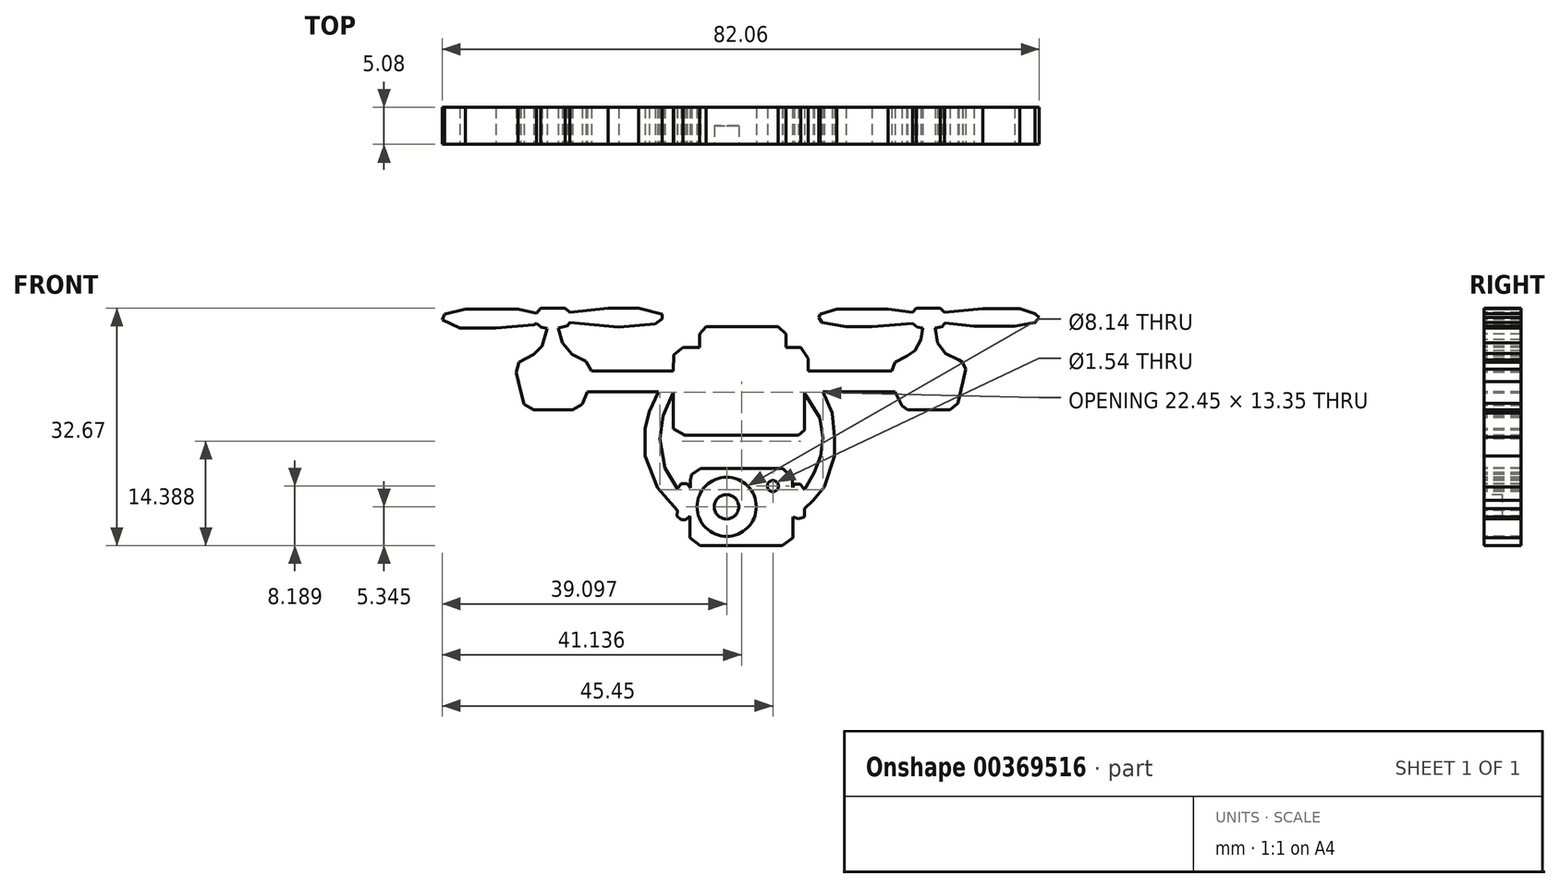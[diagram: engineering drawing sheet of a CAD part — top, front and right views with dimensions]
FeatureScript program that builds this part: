
annotation { "Feature Type Name" : "Feature", "Feature Type Description" : "" }
export const myFeature = defineFeature(function(context is Context, id is Id, definition is map)
    precondition{}
    {
        {
            var Q0;
            Q0=qCreatedBy(makeId("Front.planeOp"),FACE);
            var sketch = newSketch(context, id + "F0", { "sketchPlane" : qUnion([Q0])});
            skLineSegment(sketch, "E0", {"start": v(-9.35, 25.61) * mm, "end": v(-20.58, 25.61) * mm});
            skLineSegment(sketch, "E1", {"start": v(9.2, 25.61) * mm, "end": v(20.72, 25.61) * mm});
            skLineSegment(sketch, "E2", {"start": v(21.15, 22.74) * mm, "end": v(11.22, 22.74) * mm});
            skLineSegment(sketch, "E3", {"start": v(-11.37, 22.74) * mm, "end": v(-21.15, 22.74) * mm});
            skLineSegment(sketch, "E4", {"start": v(-23.17, 20.3) * mm, "end": v(-28.5, 20.3) * mm});
            skLineSegment(sketch, "E5", {"start": v(7.91, 16.77) * mm, "end": v(-7.76, 16.77) * mm});
            skLineSegment(sketch, "E6", {"start": v(9.2, 25.61) * mm, "end": v(9.2, 27.35) * mm});
            skLineSegment(sketch, "E7", {"start": v(9.2, 27.35) * mm, "end": v(8.22, 28.88) * mm});
            skLineSegment(sketch, "E8", {"start": v(8.22, 28.88) * mm, "end": v(6.18, 28.88) * mm});
            skLineSegment(sketch, "E9", {"start": v(6.18, 28.88) * mm, "end": v(6.18, 30.7) * mm});
            skLineSegment(sketch, "E10", {"start": v(6.18, 30.7) * mm, "end": v(5.06, 31.73) * mm});
            skLineSegment(sketch, "E11", {"start": v(5.06, 31.73) * mm, "end": v(-4.8, 31.73) * mm});
            skLineSegment(sketch, "E12", {"start": v(-4.8, 31.73) * mm, "end": v(-5.72, 30.7) * mm});
            skLineSegment(sketch, "E13", {"start": v(-5.72, 30.7) * mm, "end": v(-5.72, 28.88) * mm});
            skLineSegment(sketch, "E14", {"start": v(-5.72, 28.88) * mm, "end": v(-7.96, 28.88) * mm});
            skLineSegment(sketch, "E15", {"start": v(-7.96, 28.88) * mm, "end": v(-9.28, 27.86) * mm});
            skLineSegment(sketch, "E16", {"start": v(-9.28, 27.86) * mm, "end": v(-9.35, 25.61) * mm});
            skLineSegment(sketch, "E17", {"start": v(-7.76, 16.77) * mm, "end": v(-9.32, 17.68) * mm});
            skPoint(sketch, "E17.endSnap0", {"position": v(-9.32, 26.74) * mm});
            skLineSegment(sketch, "E18", {"start": v(-9.32, 17.68) * mm, "end": v(-9.32, 22.67) * mm});
            skLineSegment(sketch, "E19", {"start": v(-11.37, 22.74) * mm, "end": v(-12.64, 20.03) * mm});
            skLineSegment(sketch, "E20", {"start": v(-7.05, 5.68) * mm, "end": v(-7.05, 2.73) * mm});
            skLineSegment(sketch, "E21", {"start": v(-7.05, 2.73) * mm, "end": v(-5.62, 1.6) * mm});
            skLineSegment(sketch, "E22", {"start": v(-5.62, 1.6) * mm, "end": v(5.67, 1.6) * mm});
            skLineSegment(sketch, "E23", {"start": v(5.67, 1.6) * mm, "end": v(7.1, 2.73) * mm});
            skLineSegment(sketch, "E24", {"start": v(7.1, 2.73) * mm, "end": v(7.1, 5.58) * mm});
            skLineSegment(sketch, "E25", {"start": v(11.22, 22.74) * mm, "end": v(12.55, 19.85) * mm});
            skLineSegment(sketch, "E26", {"start": v(11.45, 9.68) * mm, "end": v(12.85, 13.92) * mm});
            skLineSegment(sketch, "E27", {"start": v(12.85, 13.92) * mm, "end": v(12.85, 16.52) * mm});
            skLineSegment(sketch, "E28", {"start": v(12.85, 16.52) * mm, "end": v(12.55, 19.85) * mm});
            skLineSegment(sketch, "E29", {"start": v(8.74, 9.32) * mm, "end": v(10.07, 11.62) * mm});
            skLineSegment(sketch, "E30", {"start": v(10.07, 11.62) * mm, "end": v(10.92, 13.92) * mm});
            skLineSegment(sketch, "E31", {"start": v(8.7, 22.54) * mm, "end": v(10.8, 19.19) * mm});
            skLineSegment(sketch, "E32", {"start": v(10.8, 19.19) * mm, "end": v(11.28, 16.4) * mm});
            skLineSegment(sketch, "E33", {"start": v(11.28, 16.4) * mm, "end": v(10.92, 13.92) * mm});
            skLineSegment(sketch, "E34", {"start": v(-12.64, 20.03) * mm, "end": v(-13.22, 17.68) * mm});
            skLineSegment(sketch, "E35", {"start": v(-13.22, 17.68) * mm, "end": v(-13.22, 13.92) * mm});
            skLineSegment(sketch, "E36", {"start": v(-13.22, 13.92) * mm, "end": v(-11.47, 9.57) * mm});
            skLineSegment(sketch, "E37", {"start": v(-11.47, 9.57) * mm, "end": v(-8.75, 6.42) * mm});
            skLineSegment(sketch, "E38", {"start": v(-8.75, 9.45) * mm, "end": v(-10.44, 12.29) * mm});
            skLineSegment(sketch, "E39", {"start": v(-10.44, 12.29) * mm, "end": v(-11.17, 16.28) * mm});
            skLineSegment(sketch, "E40", {"start": v(-11.17, 16.28) * mm, "end": v(-10.74, 19.43) * mm});
            skLineSegment(sketch, "E41", {"start": v(-10.74, 19.43) * mm, "end": v(-9.32, 22.67) * mm});
            skLineSegment(sketch, "E42", {"start": v(-6.98, 9.57) * mm, "end": v(-7.45, 10.11) * mm});
            skLineSegment(sketch, "E43", {"start": v(-7.45, 10.11) * mm, "end": v(-8.24, 10.11) * mm});
            skLineSegment(sketch, "E44", {"start": v(-8.24, 10.11) * mm, "end": v(-8.75, 9.45) * mm});
            skLineSegment(sketch, "E45", {"start": v(-7.05, 5.68) * mm, "end": v(-7.6, 5.19) * mm});
            skLineSegment(sketch, "E46", {"start": v(-7.6, 5.19) * mm, "end": v(-8.24, 5.19) * mm});
            skLineSegment(sketch, "E47", {"start": v(-8.24, 5.19) * mm, "end": v(-8.82, 5.68) * mm});
            skLineSegment(sketch, "E48", {"start": v(-8.82, 5.68) * mm, "end": v(-8.75, 6.42) * mm});
            skLineSegment(sketch, "E49", {"start": v(8.74, 9.32) * mm, "end": v(8.16, 10.07) * mm});
            skLineSegment(sketch, "E50", {"start": v(8.16, 10.07) * mm, "end": v(7.3, 10.07) * mm});
            skLineSegment(sketch, "E51", {"start": v(7.3, 10.07) * mm, "end": v(7.03, 9.6) * mm});
            skLineSegment(sketch, "E52", {"start": v(5.72, 12.24) * mm, "end": v(-5.58, 12.24) * mm});
            skLineSegment(sketch, "E53", {"start": v(-5.58, 12.24) * mm, "end": v(-6.77, 11.37) * mm});
            skLineSegment(sketch, "E54", {"start": v(-6.98, 9.57) * mm, "end": v(-6.98, 10.62) * mm});
            skLineSegment(sketch, "E55", {"start": v(-6.98, 10.62) * mm, "end": v(-6.77, 11.37) * mm});
            skLineSegment(sketch, "E56", {"start": v(7.03, 9.6) * mm, "end": v(7.03, 10.9) * mm});
            skLineSegment(sketch, "E57", {"start": v(7.03, 10.9) * mm, "end": v(5.72, 12.24) * mm});
            skLineSegment(sketch, "E58", {"start": v(8.7, 5.58) * mm, "end": v(7.9, 5.28) * mm});
            skLineSegment(sketch, "E59", {"start": v(7.9, 5.28) * mm, "end": v(7.1, 5.58) * mm});
            skLineSegment(sketch, "E60", {"start": v(7.91, 16.77) * mm, "end": v(8.7, 17.52) * mm});
            skLineSegment(sketch, "E61", {"start": v(8.7, 22.54) * mm, "end": v(8.7, 17.52) * mm});
            skLineSegment(sketch, "E62", {"start": v(8.7, 5.58) * mm, "end": v(8.7, 6.73) * mm});
            skLineSegment(sketch, "E63", {"start": v(-23.17, 20.3) * mm, "end": v(-21.8, 21.06) * mm});
            skLineSegment(sketch, "E64", {"start": v(-21.8, 21.06) * mm, "end": v(-21.15, 22.74) * mm});
            skLineSegment(sketch, "E65", {"start": v(-28.5, 20.3) * mm, "end": v(-29.84, 21.06) * mm});
            skLineSegment(sketch, "E66", {"start": v(-29.84, 21.06) * mm, "end": v(-30.3, 22.74) * mm});
            skLineSegment(sketch, "E67", {"start": v(-30.3, 22.74) * mm, "end": v(-30.9, 25.44) * mm});
            skLineSegment(sketch, "E68", {"start": v(-30.9, 25.44) * mm, "end": v(-30.55, 26.81) * mm});
            skLineSegment(sketch, "E69", {"start": v(-30.55, 26.81) * mm, "end": v(-28.5, 27.88) * mm});
            skLineSegment(sketch, "E70", {"start": v(-28.5, 27.88) * mm, "end": v(-27.34, 29.05) * mm});
            skLineSegment(sketch, "E71", {"start": v(-27.34, 29.05) * mm, "end": v(-26.68, 31.44) * mm});
            skLineSegment(sketch, "E72", {"start": v(-28.5, 31.94) * mm, "end": v(-33.7, 31.54) * mm});
            skLineSegment(sketch, "E73", {"start": v(-33.7, 31.54) * mm, "end": v(-38.64, 31.54) * mm});
            skLineSegment(sketch, "E74", {"start": v(-38.64, 31.54) * mm, "end": v(-41.08, 32.66) * mm});
            skLineSegment(sketch, "E75", {"start": v(-41.08, 32.66) * mm, "end": v(-40.73, 33.43) * mm});
            skLineSegment(sketch, "E76", {"start": v(-40.73, 33.43) * mm, "end": v(-37.88, 34.14) * mm});
            skLineSegment(sketch, "E77", {"start": v(-37.88, 34.14) * mm, "end": v(-30.65, 34.14) * mm});
            skLineSegment(sketch, "E78", {"start": v(-30.65, 34.14) * mm, "end": v(-26.38, 33.17) * mm});
            skLineSegment(sketch, "E79", {"start": v(-20.58, 25.61) * mm, "end": v(-21.34, 26.97) * mm});
            skLineSegment(sketch, "E80", {"start": v(-21.34, 26.97) * mm, "end": v(-23.22, 27.88) * mm});
            skLineSegment(sketch, "E81", {"start": v(-23.22, 27.88) * mm, "end": v(-24.55, 29.5) * mm});
            skLineSegment(sketch, "E82", {"start": v(-24.55, 29.5) * mm, "end": v(-25.1, 31.5) * mm});
            skLineSegment(sketch, "E83", {"start": v(-25.1, 31.5) * mm, "end": v(-23.88, 31.84) * mm});
            skPoint(sketch, "E83.endSnap0", {"position": v(-23.88, 28.7) * mm});
            skLineSegment(sketch, "E84", {"start": v(-23.58, 33.68) * mm, "end": v(-18.29, 34.24) * mm});
            skLineSegment(sketch, "E85", {"start": v(-18.29, 34.24) * mm, "end": v(-14.06, 34.24) * mm});
            skLineSegment(sketch, "E86", {"start": v(-14.06, 34.24) * mm, "end": v(-10.86, 33.43) * mm});
            skLineSegment(sketch, "E87", {"start": v(-10.86, 33.43) * mm, "end": v(-10.86, 32.77) * mm});
            skLineSegment(sketch, "E88", {"start": v(-10.86, 32.77) * mm, "end": v(-11.78, 32.1) * mm});
            skLineSegment(sketch, "E89", {"start": v(-11.78, 32.1) * mm, "end": v(-16.81, 31.65) * mm});
            skLineSegment(sketch, "E90", {"start": v(-16.81, 31.65) * mm, "end": v(-23.53, 32.26) * mm});
            skLineSegment(sketch, "E91", {"start": v(-23.88, 31.84) * mm, "end": v(-23.53, 32.26) * mm});
            skLineSegment(sketch, "E92", {"start": v(-23.58, 33.68) * mm, "end": v(-24.18, 34.25) * mm});
            skLineSegment(sketch, "E93", {"start": v(-24.18, 34.25) * mm, "end": v(-27.52, 34.25) * mm});
            skLineSegment(sketch, "E94", {"start": v(-27.52, 34.25) * mm, "end": v(-28.14, 33.57) * mm});
            skLineSegment(sketch, "E95", {"start": v(20.72, 25.61) * mm, "end": v(21.15, 26.84) * mm});
            skLineSegment(sketch, "E96", {"start": v(21.15, 26.84) * mm, "end": v(22.77, 27.63) * mm});
            skLineSegment(sketch, "E97", {"start": v(22.77, 27.63) * mm, "end": v(23.89, 28.42) * mm});
            skLineSegment(sketch, "E98", {"start": v(23.89, 28.42) * mm, "end": v(24.72, 29.93) * mm});
            skLineSegment(sketch, "E99", {"start": v(24.72, 29.93) * mm, "end": v(24.97, 31.51) * mm});
            skLineSegment(sketch, "E100", {"start": v(24.97, 31.51) * mm, "end": v(24.22, 31.63) * mm});
            skLineSegment(sketch, "E101", {"start": v(24.22, 31.63) * mm, "end": v(23.56, 32.16) * mm});
            skLineSegment(sketch, "E102", {"start": v(23.56, 32.16) * mm, "end": v(17.99, 31.7) * mm});
            skLineSegment(sketch, "E103", {"start": v(17.99, 31.7) * mm, "end": v(14.43, 31.7) * mm});
            skLineSegment(sketch, "E104", {"start": v(14.43, 31.7) * mm, "end": v(11.15, 32.27) * mm});
            skLineSegment(sketch, "E105", {"start": v(11.15, 32.27) * mm, "end": v(10.65, 32.95) * mm});
            skPoint(sketch, "E106.endSnap0", {"position": v(10.9, 32.61) * mm});
            skLineSegment(sketch, "E107", {"start": v(-26.38, 33.17) * mm, "end": v(-26.33, 32.77) * mm});
            skLineSegment(sketch, "E108", {"start": v(23.56, 33.67) * mm, "end": v(20.22, 34.1) * mm});
            skLineSegment(sketch, "E109", {"start": v(20.22, 34.1) * mm, "end": v(15.76, 34.1) * mm});
            skLineSegment(sketch, "E110", {"start": v(15.76, 34.1) * mm, "end": v(13.13, 34.1) * mm});
            skLineSegment(sketch, "E111", {"start": v(13.13, 34.1) * mm, "end": v(10.9, 33.42) * mm});
            skLineSegment(sketch, "E112", {"start": v(10.9, 33.42) * mm, "end": v(10.65, 32.95) * mm});
            skLineSegment(sketch, "E113", {"start": v(23.56, 33.67) * mm, "end": v(24.1, 34.28) * mm});
            skLineSegment(sketch, "E114", {"start": v(24.1, 34.28) * mm, "end": v(27.38, 34.28) * mm});
            skLineSegment(sketch, "E115", {"start": v(27.38, 34.28) * mm, "end": v(27.95, 33.67) * mm});
            skLineSegment(sketch, "E116", {"start": v(27.95, 33.67) * mm, "end": v(33.24, 34.18) * mm});
            skLineSegment(sketch, "E117", {"start": v(33.24, 34.18) * mm, "end": v(38.28, 34.18) * mm});
            skLineSegment(sketch, "E118", {"start": v(28.03, 32.2) * mm, "end": v(32.02, 31.77) * mm});
            skLineSegment(sketch, "E119", {"start": v(32.02, 31.77) * mm, "end": v(37.6, 31.77) * mm});
            skLineSegment(sketch, "E120", {"start": v(37.6, 31.77) * mm, "end": v(40.4, 32.3) * mm});
            skLineSegment(sketch, "E121", {"start": v(40.4, 32.3) * mm, "end": v(40.98, 32.99) * mm});
            skLineSegment(sketch, "E122", {"start": v(40.98, 32.99) * mm, "end": v(40.4, 33.47) * mm});
            skLineSegment(sketch, "E123", {"start": v(40.4, 33.47) * mm, "end": v(38.28, 34.18) * mm});
            skLineSegment(sketch, "E124", {"start": v(26.7, 31.55) * mm, "end": v(27.02, 29.46) * mm});
            skLineSegment(sketch, "E125", {"start": v(27.02, 29.46) * mm, "end": v(28.06, 28.06) * mm});
            skLineSegment(sketch, "E126", {"start": v(28.06, 28.06) * mm, "end": v(29.9, 27.16) * mm});
            skLineSegment(sketch, "E127", {"start": v(26.7, 31.55) * mm, "end": v(27.6, 31.7) * mm});
            skLineSegment(sketch, "E128", {"start": v(27.6, 31.7) * mm, "end": v(28.03, 32.2) * mm});
            skLineSegment(sketch, "E129", {"start": v(21.15, 22.74) * mm, "end": v(22.13, 20.87) * mm});
            skLineSegment(sketch, "E130", {"start": v(22.13, 20.87) * mm, "end": v(22.88, 20.25) * mm});
            skLineSegment(sketch, "E131", {"start": v(22.88, 20.25) * mm, "end": v(28.74, 20.25) * mm});
            skLineSegment(sketch, "E132", {"start": v(28.74, 20.25) * mm, "end": v(29.82, 21.19) * mm});
            skLineSegment(sketch, "E133", {"start": v(29.82, 21.19) * mm, "end": v(30.47, 24.18) * mm});
            skLineSegment(sketch, "E134", {"start": v(30.47, 24.18) * mm, "end": v(30.9, 25.9) * mm});
            skLineSegment(sketch, "E135", {"start": v(30.9, 25.9) * mm, "end": v(30.44, 26.8) * mm});
            skLineSegment(sketch, "E136", {"start": v(30.44, 26.8) * mm, "end": v(29.9, 27.16) * mm});
            skLineSegment(sketch, "E137", {"start": v(23.56, 32.16) * mm, "end": v(25.1, 32.6) * mm});
            skLineSegment(sketch, "E138", {"start": v(23.56, 33.67) * mm, "end": v(25.1, 33.27) * mm});
            skLineSegment(sketch, "E139", {"start": v(25.1, 33.27) * mm, "end": v(25.1, 32.6) * mm});
            skLineSegment(sketch, "E140", {"start": v(-26.68, 31.44) * mm, "end": v(-27.5, 31.67) * mm});
            skLineSegment(sketch, "E141", {"start": v(-27.5, 31.67) * mm, "end": v(-28.14, 32.15) * mm});
            skLineSegment(sketch, "E142", {"start": v(-28.14, 32.15) * mm, "end": v(-28.5, 31.94) * mm});
            skLineSegment(sketch, "E143", {"start": v(-28.14, 32.15) * mm, "end": v(-26.33, 32.77) * mm});
            skLineSegment(sketch, "E144", {"start": v(-7.05, 5.68) * mm, "end": v(-6.98, 9.57) * mm});
            skLineSegment(sketch, "E145", {"start": v(7.1, 5.58) * mm, "end": v(7.03, 9.6) * mm});
            skCircle(sketch, "E146", {"center": v(-1.98, 6.96) * mm, "radius": 3.28 * mm});
            skCircle(sketch, "E147", {"center": v(-1.98, 6.96) * mm, "radius": 4.07 * mm});
            skCircle(sketch, "E148", {"center": v(4.37, 9.8) * mm, "radius": 0.77 * mm});
            skLineSegment(sketch, "E149", {"start": v(-8.75, 6.42) * mm, "end": v(-8.75, 9.45) * mm});
            skLineSegment(sketch, "E150", {"start": v(8.7, 22.54) * mm, "end": v(11.22, 22.74) * mm});
            skLineSegment(sketch, "E151", {"start": v(-11.37, 22.74) * mm, "end": v(-9.32, 22.67) * mm});
            skLineSegment(sketch, "E152", {"start": v(8.7, 22.54) * mm, "end": v(9.2, 25.61) * mm});
            skLineSegment(sketch, "E153", {"start": v(-9.32, 22.67) * mm, "end": v(-9.35, 25.61) * mm});
            skLineSegment(sketch, "E154", {"start": v(21.15, 22.74) * mm, "end": v(20.72, 25.61) * mm});
            skLineSegment(sketch, "E155", {"start": v(-21.15, 22.74) * mm, "end": v(-20.58, 25.61) * mm});
            skLineSegment(sketch, "E156", {"start": v(-8.75, 9.45) * mm, "end": v(-7.76, 16.77) * mm});
            skCircle(sketch, "E157", {"center": v(-3.1, 8.13) * mm, "radius": 1.15 * mm});
            skLineSegment(sketch, "E158", {"start": v(7.3, 10.07) * mm, "end": v(8.7, 17.52) * mm});
            skLineSegment(sketch, "E159", {"start": v(8.7, 6.73) * mm, "end": v(9.9, 7.83) * mm});
            skLineSegment(sketch, "E160", {"start": v(9.9, 7.83) * mm, "end": v(11.45, 9.68) * mm});
            skSolve(sketch);
        }
        {
            var Q0;
            Q0 = qSketchRegion(id + "F0", true);
            extrude(context, id + "F1", {"entities" : qUnion([Q0]), "oppositeDirection" : true, "depth" : 5.08 * mm});
        }
        {
            var Q0;
            Q0=qCreatedBy(makeId("Front.planeOp"),FACE);
            var sketch = newSketch(context, id + "F2", { "sketchPlane" : qUnion([Q0])});
            skCircle(sketch, "E161", {"center": v(-2, 6.95) * mm, "radius": 1.68 * mm});
            skSolve(sketch);
        }
        {
            var Q0;
            Q0=makeQuery(id+"F2.imprint","IMPRINT",FACE,{"disambiguationData":[TD([[makeQuery(id+"F2.imprint","IMPRINT",EDGE,{"derivedFrom":sQuery(id+"F2.wireOp",EDGE,"E161")}),1.0]])]});
            var Q1;
            Q1=sQuery(id+"F2.wireOp",EDGE,"CNlkC5pD-uHCq-TDT1-wmio-CYf8QKGe3G23");
            var Q2;
            Q2=sQuery(id+"F2.wireOp",EDGE,"E161");
            extrude(context, id + "F3", {"entities" : qUnion([Q0]), "surfaceEntities" : qUnion([Q1, Q2]), "oppositeDirection" : true, "depth" : 2.54 * mm});
        }
    });
